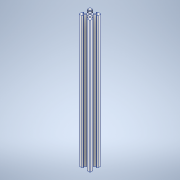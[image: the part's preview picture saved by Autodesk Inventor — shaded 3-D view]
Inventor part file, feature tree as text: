
AUTODESK INVENTOR PART (.ipt)
format: ipt  version: 2021 (Build 250183000, 183)  size: 236,032 bytes
history: native  units: mm
features: sketch x3, extrude x2, fillet x2, other x1, pattern_circular x1, hole x1, projected_geometry x1
ambient origin geometry x8: Origin, YZ Plane, XZ Plane, XY Plane, X Axis, Y Axis, Z Axis, Center Point
bodies: Body1 (feature_tree)
feature tree (11):
  other  "實體1"
  extrude  "擠出1"  Depth=20.0mm
  extrude  "擠出2"  Depth=20.0mm
  fillet  "圓角1"  Radius=240.0mm
  pattern_circular  "環形陣列1"  [2 undecoded]
  hole  "孔1"  [1 undecoded]
  fillet  "圓角2"  Radius=6.2mm
  sketch  "草圖1"
  sketch  "草圖2"
  projected_geometry  "投影迴路1"
  sketch  "草圖3"
note: 3 required parameter values undecoded (feature->parameter linkage not recoverable at this tier; creation-order binding heuristic only, values carry confidence <= 0.55)
